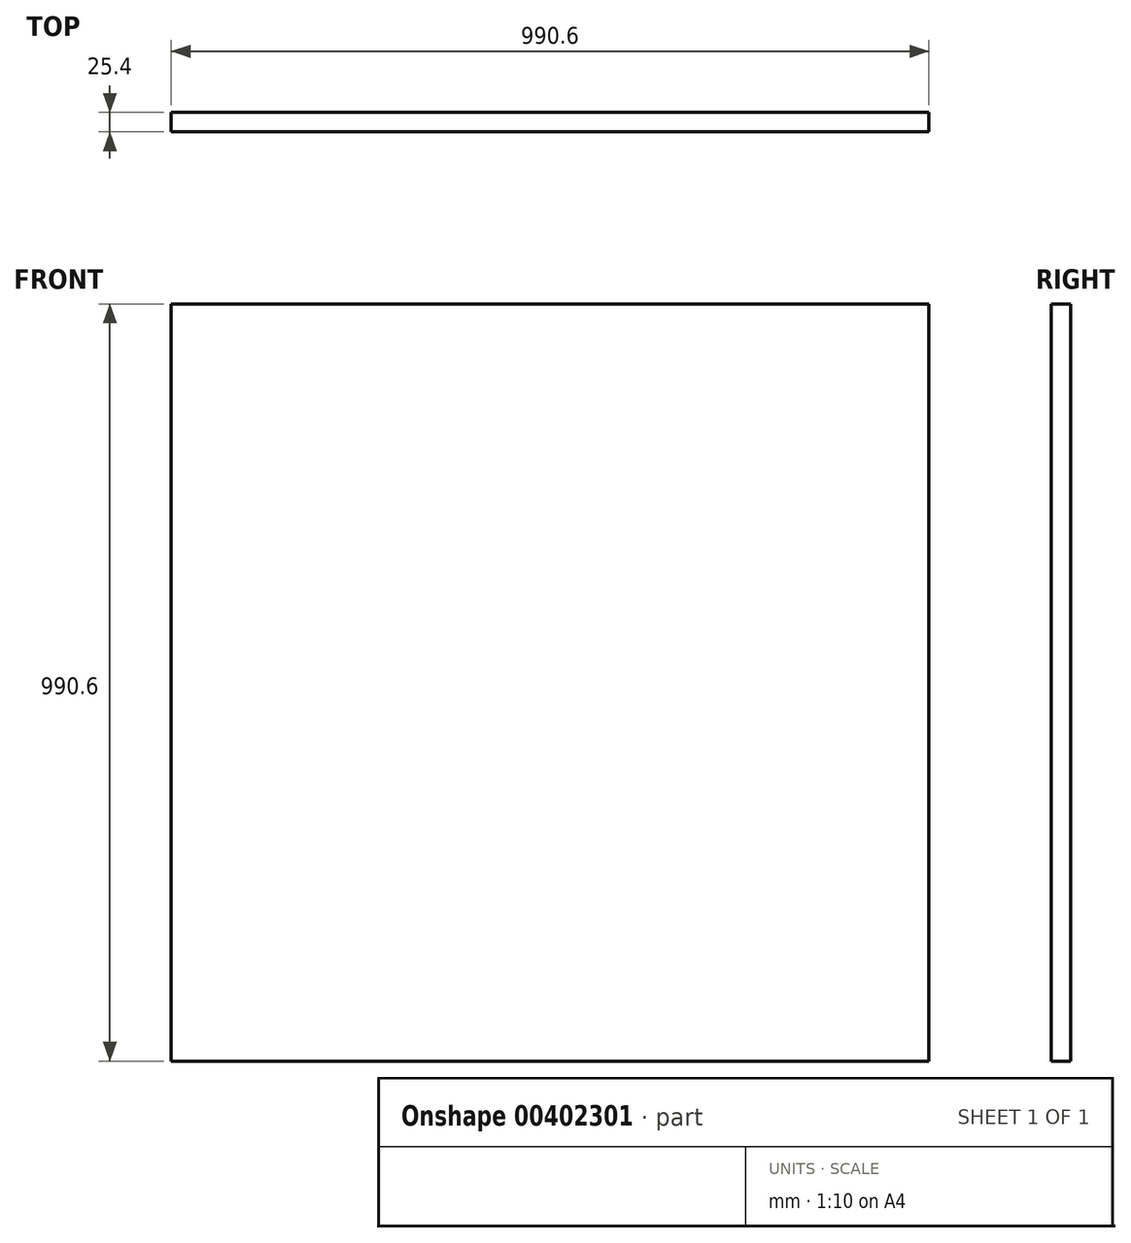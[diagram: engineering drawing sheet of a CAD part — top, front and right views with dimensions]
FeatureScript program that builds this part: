
annotation { "Feature Type Name" : "Feature", "Feature Type Description" : "" }
export const myFeature = defineFeature(function(context is Context, id is Id, definition is map)
    precondition{}
    {
        {
            var Q0;
            Q0=qCreatedBy(makeId("Front.planeOp"),FACE);
            var sketch = newSketch(context, id + "F0", { "sketchPlane" : qUnion([Q0])});
            skLineSegment(sketch, "E0.bottom", {"start": v(-495.3, 495.3) * mm, "end": v(495.3, 495.3) * mm});
            skLineSegment(sketch, "E0.top", {"start": v(-495.3, -495.3) * mm, "end": v(495.3, -495.3) * mm});
            skLineSegment(sketch, "E0.left", {"start": v(-495.3, 495.3) * mm, "end": v(-495.3, -495.3) * mm});
            skLineSegment(sketch, "E0.right", {"start": v(495.3, 495.3) * mm, "end": v(495.3, -495.3) * mm});
            skPoint(sketch, "E0.middle", {"position": v(0, 0) * mm});
            skSolve(sketch);
        }
        {
            var Q0;
            Q0 = qSketchRegion(id + "F0", true);
            extrude(context, id + "F1", {"entities" : qUnion([Q0]), "depth" : 25.4 * mm});
        }
    });
